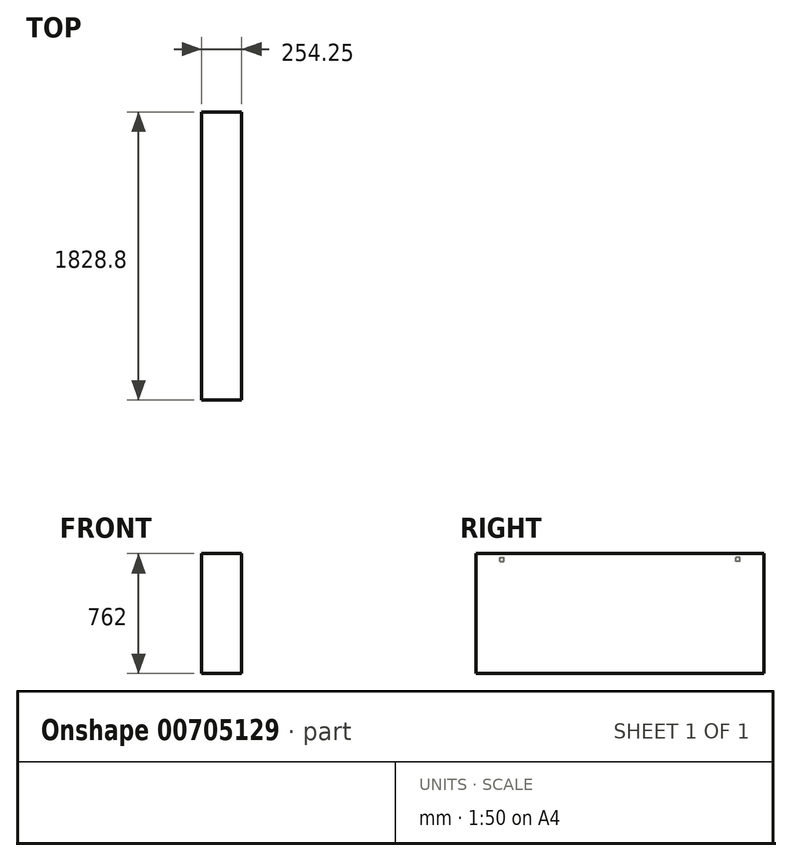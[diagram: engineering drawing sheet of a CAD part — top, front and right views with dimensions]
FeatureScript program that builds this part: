
annotation { "Feature Type Name" : "Feature", "Feature Type Description" : "" }
export const myFeature = defineFeature(function(context is Context, id is Id, definition is map)
    precondition{}
    {
        {
            var Q0;
            Q0=qCreatedBy(makeId("Front.planeOp"),FACE);
            var sketch = newSketch(context, id + "F0", { "sketchPlane" : qUnion([Q0])});
            skLineSegment(sketch, "E0.bottom", {"start": v(127, -381) * mm, "end": v(-127, -381) * mm});
            skLineSegment(sketch, "E0.top", {"start": v(127, 381) * mm, "end": v(-127, 381) * mm});
            skLineSegment(sketch, "E0.left", {"start": v(127, -381) * mm, "end": v(127, 381) * mm});
            skLineSegment(sketch, "E0.right", {"start": v(-127, -381) * mm, "end": v(-127, 381) * mm});
            skPoint(sketch, "E0.middle", {"position": v(0, 0) * mm});
            skSolve(sketch);
        }
        {
            var Q0;
            Q0 = qSketchRegion(id + "F0", true);
            extrude(context, id + "F1", {"entities" : qUnion([Q0]), "endBound" : BoundingType.SYMMETRIC, "depth" : 1828.8 * mm, "offsetDistance" : 25.4 * mm});
        }
        {
            var Q0;
            Q0=makeQuery(id+"F1.opExtrude","SWEPT_FACE",FACE,{"disambiguationData":[OSD([sQuery(id+"F0.wireOp",EDGE,"E0.right")])]});
            var sketch = newSketch(context, id + "F2", { "sketchPlane" : qUnion([Q0])});
            skLineSegment(sketch, "E1.bottom", {"start": v(762, 330.2) * mm, "end": v(736.6, 330.2) * mm});
            skLineSegment(sketch, "E1.top", {"start": v(762, 355.6) * mm, "end": v(736.6, 355.6) * mm});
            skLineSegment(sketch, "E1.left", {"start": v(762, 330.2) * mm, "end": v(762, 355.6) * mm});
            skLineSegment(sketch, "E1.right", {"start": v(736.6, 330.2) * mm, "end": v(736.6, 355.6) * mm});
            skLineSegment(sketch, "E2.bottom", {"start": v(-762, 330.2) * mm, "end": v(-736.6, 330.2) * mm});
            skLineSegment(sketch, "E2.top", {"start": v(-762, 355.6) * mm, "end": v(-736.6, 355.6) * mm});
            skLineSegment(sketch, "E2.left", {"start": v(-762, 330.2) * mm, "end": v(-762, 355.6) * mm});
            skLineSegment(sketch, "E2.right", {"start": v(-736.6, 330.2) * mm, "end": v(-736.6, 355.6) * mm});
            skSolve(sketch);
        }
        {
            var Q0;
            Q0 = qSketchRegion(id + "F2", true);
            extrude(context, id + "F3", {"entities" : qUnion([Q0]), "operationType" : NewBodyOperationType.ADD, "depth" : 0.25 * mm, "offsetDistance" : 25.4 * mm});
        }
    });
